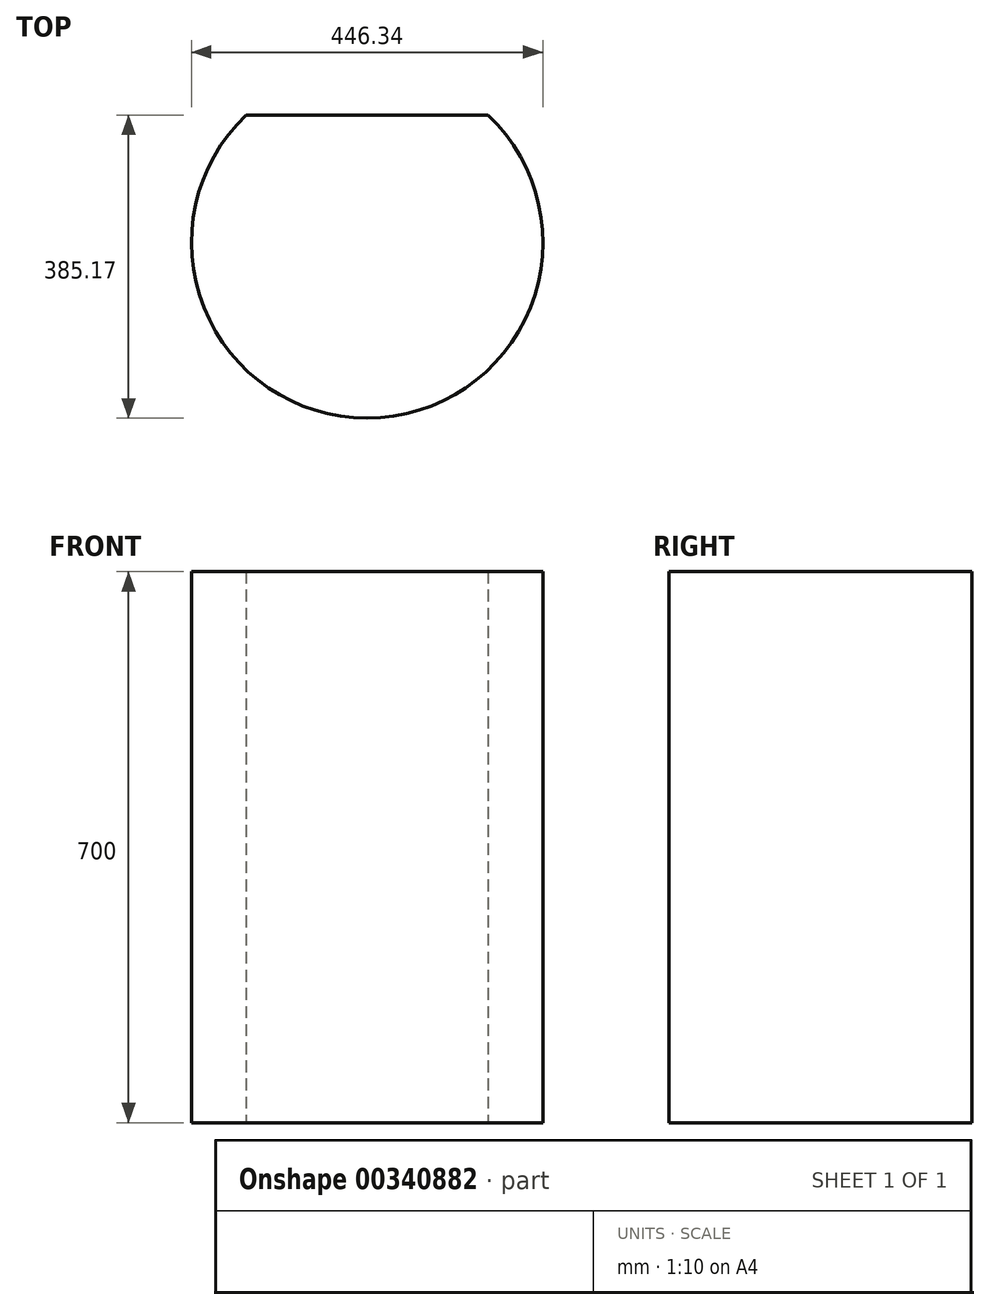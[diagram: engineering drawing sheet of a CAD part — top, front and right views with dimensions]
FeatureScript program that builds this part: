
annotation { "Feature Type Name" : "Feature", "Feature Type Description" : "" }
export const myFeature = defineFeature(function(context is Context, id is Id, definition is map)
    precondition{}
    {
        {
            var Q0;
            Q0=qCreatedBy(makeId("Top.planeOp"),FACE);
            var sketch = newSketch(context, id + "F0", { "sketchPlane" : qUnion([Q0])});
            skCircle(sketch, "E0", {"center": v(0, 0) * mm, "radius": 223.17 * mm});
            skLineSegment(sketch, "E1", {"start": v(-153.5, 162) * mm, "end": v(153.5, 162) * mm});
            skSolve(sketch);
        }
        {
            var Q0;
            {var subQ0=sQuery(id+"F0.wireOp",EDGE,"E1");Q0=makeQuery(id+"F0.imprint","IMPRINT",FACE,{"disambiguationData":[TD([[makeQuery(id+"F0.imprint","IMPRINT",EDGE,{"derivedFrom":subQ0}),-1.0]])]});}
            extrude(context, id + "F1", {"entities" : qUnion([Q0]), "depth" : 700 * mm});
        }
    });
